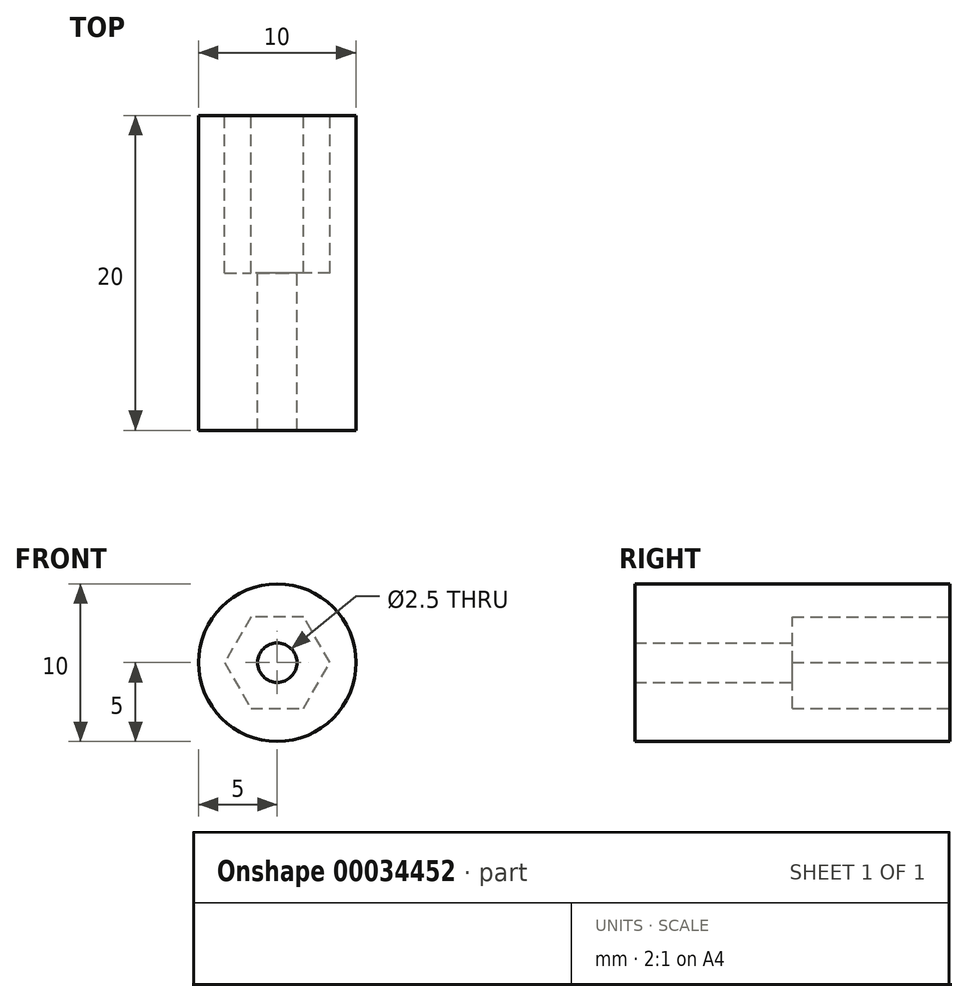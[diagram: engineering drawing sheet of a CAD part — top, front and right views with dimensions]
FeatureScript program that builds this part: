
annotation { "Feature Type Name" : "Feature", "Feature Type Description" : "" }
export const myFeature = defineFeature(function(context is Context, id is Id, definition is map)
    precondition{}
    {
        {
            var Q0;
            Q0=qCreatedBy(makeId("Front.planeOp"),FACE);
            var sketch = newSketch(context, id + "F0", { "sketchPlane" : qUnion([Q0])});
            skCircle(sketch, "E0", {"center": v(0, 0) * mm, "radius": 5 * mm});
            skSolve(sketch);
        }
        {
            var Q0;
            Q0 = qSketchRegion(id + "F0", true);
            extrude(context, id + "F1", {"entities" : qUnion([Q0]), "depth" : 20 * mm});
        }
        {
            var Q0;
            Q0=makeQuery(id+"F1.opExtrude","CAP_FACE",FACE,{"disambiguationData":[OSD([sQuery(id+"F0.wireOp",EDGE,"E0")])],"isStart":true});
            var sketch = newSketch(context, id + "F2", { "sketchPlane" : qUnion([Q0])});
            skCircle(sketch, "E1", {"center": v(0, 0) * mm, "radius": 1.25 * mm});
            skSolve(sketch);
        }
        {
            var Q0;
            Q0 = qSketchRegion(id + "F2", true);
            extrude(context, id + "F3", {"entities" : qUnion([Q0]), "operationType" : NewBodyOperationType.REMOVE, "endBound" : BoundingType.THROUGH_ALL, "oppositeDirection" : true, "depth" : 25.4 * mm});
        }
        {
            var Q0;
            Q0=qCreatedBy(makeId("Front.planeOp"),FACE);
            var sketch = newSketch(context, id + "F4", { "sketchPlane" : qUnion([Q0])});
            skCircle(sketch, "E2", {"center": v(0, 0) * mm, "radius": 2.9 * mm, "construction": true});
            skLineSegment(sketch, "E3", {"start": v(-1.67, 2.9) * mm, "end": v(-3.35, 0) * mm});
            skLineSegment(sketch, "E4", {"start": v(-3.35, 0) * mm, "end": v(-1.67, -2.9) * mm});
            skLineSegment(sketch, "E5", {"start": v(-1.67, -2.9) * mm, "end": v(1.67, -2.9) * mm});
            skLineSegment(sketch, "E6", {"start": v(1.67, -2.9) * mm, "end": v(3.35, 0) * mm});
            skLineSegment(sketch, "E7", {"start": v(3.35, 0) * mm, "end": v(1.67, 2.9) * mm});
            skLineSegment(sketch, "E8", {"start": v(1.67, 2.9) * mm, "end": v(-1.67, 2.9) * mm});
            skSolve(sketch);
        }
        {
            var Q0;
            Q0=makeQuery(id+"F4.imprint","IMPRINT",FACE,{"disambiguationData":[TD([[makeQuery(id+"F4.imprint","IMPRINT",EDGE,{"derivedFrom":sQuery(id+"F4.wireOp",EDGE,"E3")}),1.0]])]});
            extrude(context, id + "F5", {"entities" : qUnion([Q0]), "operationType" : NewBodyOperationType.REMOVE, "depth" : 10 * mm});
        }
    });
